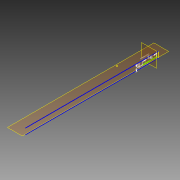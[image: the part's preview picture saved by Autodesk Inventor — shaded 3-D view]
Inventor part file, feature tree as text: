
AUTODESK INVENTOR PART (.ipt)
format: ipt  version: 2012 SP2 (Build 160219200, 219)  size: 124,928 bytes
history: native  units: in
note: dims shown in document units (in); Inventor stores cm internally (conversion verified against a paired STEP export)
features: sketch x6, extrude x3, plane x2, fillet x2, reference x2, sweep x1
ambient origin geometry x8: Origin, YZ Plane, XZ Plane, XY Plane, X Axis, Y Axis, Z Axis, Center Point
bodies: Solid1 (feature_tree)
feature tree (16):
  sketch  "Sketch2"  dims[d0=0.0787in d1=1.9685in d2=-4.375in d6=0.0in]
  plane  "Work Plane1"
  sketch  "Sketch3"  dims[d7=0.5906in d8=0.1378in]
  plane  "Work Plane2"
  sweep  "Sweep1"
  fillet  "Fillet1"  [1 undecoded]
  fillet  "Fillet2"  [1 undecoded]
  extrude  "Extrusion1"  Depth=0.1378in
  extrude  "Extrusion2"  Depth=0.0162in
  extrude  "Extrusion3"  Depth=0.3937in TaperAngle=0.0deg
  reference  "Reference1"
  reference  "Reference2"
  sketch  "Sketch4"  dims[d9=0.1412in d10=0.0162in]
  sketch  "Sketch5"  dims[d11=0.3937in d12=0.0in d13=0.3937in d14=0.0in]
  sketch  "Sketch6"  dims[d15=0.3312in d16=0.0in]
  sketch  "Sketch7"
note: 2 required parameter values undecoded (feature->parameter linkage not recoverable at this tier; creation-order binding heuristic only, values carry confidence <= 0.55)
